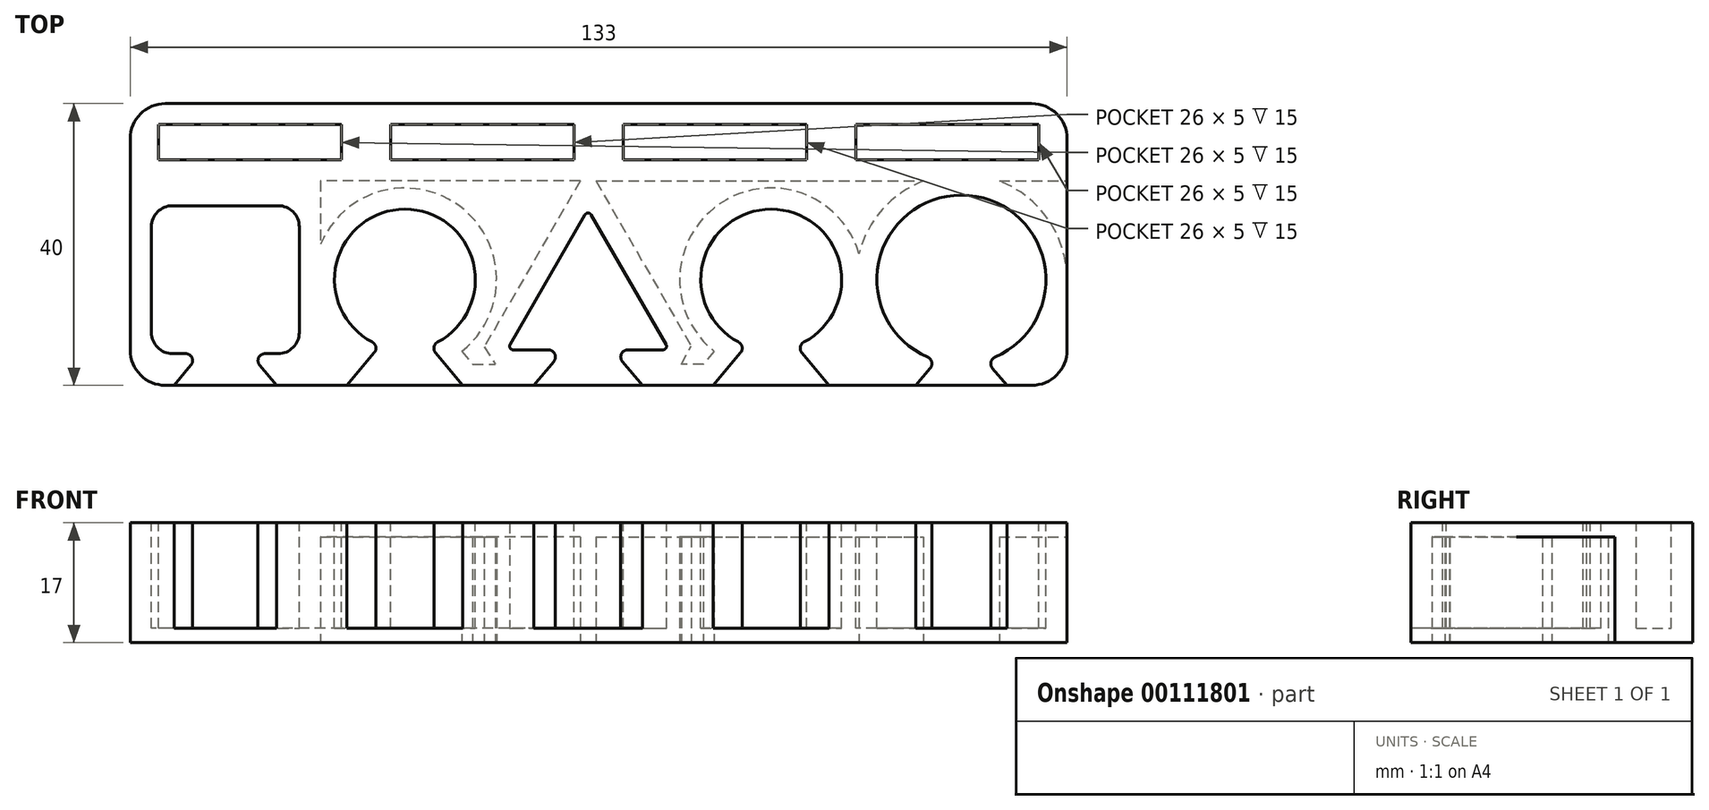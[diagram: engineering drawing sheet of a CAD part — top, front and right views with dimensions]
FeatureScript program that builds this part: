
annotation { "Feature Type Name" : "Feature", "Feature Type Description" : "" }
export const myFeature = defineFeature(function(context is Context, id is Id, definition is map)
    precondition{}
    {
        {
            var Q0;
            Q0=qCreatedBy(makeId("Top.planeOp"),FACE);
            var sketch = newSketch(context, id + "F0", { "sketchPlane" : qUnion([Q0])});
            skLineSegment(sketch, "E0.bottom", {"start": v(66.5, 20) * mm, "end": v(-66.5, 20) * mm});
            skLineSegment(sketch, "E0.top", {"start": v(66.5, -20) * mm, "end": v(-66.5, -20) * mm});
            skLineSegment(sketch, "E0.left", {"start": v(66.5, 20) * mm, "end": v(66.5, -20) * mm});
            skLineSegment(sketch, "E0.right", {"start": v(-66.5, 20) * mm, "end": v(-66.5, -20) * mm});
            skPoint(sketch, "E0.middle", {"position": v(0, 0) * mm});
            skSolve(sketch);
        }
        {
            var Q0;
            Q0=makeQuery(id+"F0.imprint","IMPRINT",FACE,{"disambiguationData":[TD([[makeQuery(id+"F0.imprint","IMPRINT",EDGE,{"derivedFrom":sQuery(id+"F0.wireOp",EDGE,"E0.bottom")}),1.0]])]});
            extrude(context, id + "F1", {"entities" : qUnion([Q0]), "depth" : 17 * mm});
        }
        {
            var Q0;
            Q0=makeQuery(id+"F1.opExtrude","CAP_FACE",FACE,{"disambiguationData":[OSD([sQuery(id+"F0.wireOp",EDGE,"E0.bottom"),sQuery(id+"F0.wireOp",EDGE,"E0.top"),sQuery(id+"F0.wireOp",EDGE,"E0.left"),sQuery(id+"F0.wireOp",EDGE,"E0.right")])],"isStart":false});
            var sketch = newSketch(context, id + "F2", { "sketchPlane" : qUnion([Q0])});
            skLineSegment(sketch, "E1.bottom", {"start": v(-36.5, 12) * mm, "end": v(-62.5, 12) * mm});
            skLineSegment(sketch, "E1.top", {"start": v(-36.5, 17) * mm, "end": v(-62.5, 17) * mm});
            skLineSegment(sketch, "E1.left", {"start": v(-36.5, 12) * mm, "end": v(-36.5, 17) * mm});
            skLineSegment(sketch, "E1.right", {"start": v(-62.5, 12) * mm, "end": v(-62.5, 17) * mm});
            skPoint(sketch, "E1.middle", {"position": v(-49.5, 14.5) * mm});
            skLineSegment(sketch, "E2.bottom", {"start": v(-3.5, 12) * mm, "end": v(-29.5, 12) * mm});
            skLineSegment(sketch, "E2.top", {"start": v(-3.5, 17) * mm, "end": v(-29.5, 17) * mm});
            skLineSegment(sketch, "E2.left", {"start": v(-3.5, 12) * mm, "end": v(-3.5, 17) * mm});
            skLineSegment(sketch, "E2.right", {"start": v(-29.5, 12) * mm, "end": v(-29.5, 17) * mm});
            skPoint(sketch, "E2.middle", {"position": v(-16.5, 14.5) * mm});
            skLineSegment(sketch, "E3.bottom", {"start": v(29.5, 12) * mm, "end": v(3.5, 12) * mm});
            skLineSegment(sketch, "E3.top", {"start": v(29.5, 17) * mm, "end": v(3.5, 17) * mm});
            skLineSegment(sketch, "E3.left", {"start": v(29.5, 12) * mm, "end": v(29.5, 17) * mm});
            skLineSegment(sketch, "E3.right", {"start": v(3.5, 12) * mm, "end": v(3.5, 17) * mm});
            skPoint(sketch, "E3.middle", {"position": v(16.5, 14.5) * mm});
            skLineSegment(sketch, "E4.bottom", {"start": v(62.5, 12) * mm, "end": v(36.5, 12) * mm});
            skLineSegment(sketch, "E4.top", {"start": v(62.5, 17) * mm, "end": v(36.5, 17) * mm});
            skLineSegment(sketch, "E4.left", {"start": v(62.5, 12) * mm, "end": v(62.5, 17) * mm});
            skLineSegment(sketch, "E4.right", {"start": v(36.5, 12) * mm, "end": v(36.5, 17) * mm});
            skPoint(sketch, "E4.middle", {"position": v(49.5, 14.5) * mm});
            skLineSegment(sketch, "E5.bottom", {"start": v(-42.5, -15.5) * mm, "end": v(-63.5, -15.5) * mm});
            skLineSegment(sketch, "E5.top", {"start": v(-42.5, 5.5) * mm, "end": v(-63.5, 5.5) * mm});
            skLineSegment(sketch, "E5.left", {"start": v(-42.5, -15.5) * mm, "end": v(-42.5, 5.5) * mm});
            skLineSegment(sketch, "E5.right", {"start": v(-63.5, -15.5) * mm, "end": v(-63.5, 5.5) * mm});
            skPoint(sketch, "E5.middle", {"position": v(-53, -5) * mm});
            skCircle(sketch, "E6", {"center": v(-27.5, -5) * mm, "radius": 10 * mm});
            skCircle(sketch, "E7", {"center": v(24.5, -5) * mm, "radius": 10 * mm});
            skCircle(sketch, "E8", {"center": v(51.5, -5) * mm, "radius": 12 * mm});
            skLineSegment(sketch, "E9", {"start": v(-13, -14.96) * mm, "end": v(10, -14.96) * mm});
            skLineSegment(sketch, "E10", {"start": v(-1.5, -14.96) * mm, "end": v(-1.5, 4.96) * mm});
            skLineSegment(sketch, "E11", {"start": v(-1.5, 4.96) * mm, "end": v(10, -14.96) * mm});
            skLineSegment(sketch, "E12", {"start": v(-1.5, 4.96) * mm, "end": v(-13, -14.96) * mm});
            skLineSegment(sketch, "E13", {"start": v(-49.5, -15.5) * mm, "end": v(-45.72, -20) * mm});
            skLineSegment(sketch, "E14", {"start": v(-56.5, -15.5) * mm, "end": v(-60.28, -20) * mm});
            skLineSegment(sketch, "E15", {"start": v(-31, -14.37) * mm, "end": v(-35.73, -20) * mm});
            skLineSegment(sketch, "E16", {"start": v(-24, -14.37) * mm, "end": v(-19.27, -20) * mm});
            skLineSegment(sketch, "E17", {"start": v(-5, -14.96) * mm, "end": v(-9.23, -20) * mm});
            skLineSegment(sketch, "E18", {"start": v(2, -14.96) * mm, "end": v(6.23, -20) * mm});
            skLineSegment(sketch, "E19", {"start": v(21, -14.37) * mm, "end": v(16.27, -20) * mm});
            skLineSegment(sketch, "E20", {"start": v(28, -14.37) * mm, "end": v(32.73, -20) * mm});
            skLineSegment(sketch, "E21", {"start": v(48, -16.48) * mm, "end": v(45.04, -20) * mm});
            skLineSegment(sketch, "E22", {"start": v(55, -16.48) * mm, "end": v(57.96, -20) * mm});
            skSolve(sketch);
        }
        {
            var Q0;
            Q0=makeQuery(id+"F2.imprint","IMPRINT",FACE,{"disambiguationData":[TD([[makeQuery(id+"F2.imprint","IMPRINT",EDGE,{"derivedFrom":sQuery(id+"F2.wireOp",EDGE,"E2.bottom")}),-1.0]])]});
            var Q1;
            Q1=makeQuery(id+"F2.imprint","IMPRINT",FACE,{"disambiguationData":[TD([[makeQuery(id+"F2.imprint","IMPRINT",EDGE,{"derivedFrom":sQuery(id+"F2.wireOp",EDGE,"E3.bottom")}),-1.0]])]});
            var Q2;
            Q2=makeQuery(id+"F2.imprint","IMPRINT",FACE,{"disambiguationData":[TD([[makeQuery(id+"F2.imprint","IMPRINT",EDGE,{"derivedFrom":sQuery(id+"F2.wireOp",EDGE,"E4.bottom")}),-1.0]])]});
            var Q3;
            Q3=makeQuery(id+"F2.imprint","IMPRINT",FACE,{"disambiguationData":[TD([[makeQuery(id+"F2.imprint","IMPRINT",EDGE,{"derivedFrom":sQuery(id+"F2.wireOp",EDGE,"E5.top")}),1.0]])]});
            var Q4;
            {var subQ0=sQuery(id+"F2.wireOp",EDGE,"E6");var subQ1=makeQuery(id+"F2.imprint","INTERSECT",VERTEX,{"derivedFrom":[subQ0,sQuery(id+"F2.wireOp",EDGE,"E15")]});Q4=makeQuery(id+"F2.imprint","IMPRINT",FACE,{"disambiguationData":[TD([[makeQuery(id+"F2.imprint","IMPRINT",EDGE,{"disambiguationData":[TD([[subQ1,-1.0]])],"derivedFrom":subQ0}),1.0]])]});}
            var Q5;
            {var subQ0=sQuery(id+"F2.wireOp",EDGE,"E7");var subQ1=makeQuery(id+"F2.imprint","INTERSECT",VERTEX,{"derivedFrom":[subQ0,sQuery(id+"F2.wireOp",EDGE,"E19")]});Q5=makeQuery(id+"F2.imprint","IMPRINT",FACE,{"disambiguationData":[TD([[makeQuery(id+"F2.imprint","IMPRINT",EDGE,{"disambiguationData":[TD([[subQ1,-1.0]])],"derivedFrom":subQ0}),1.0]])]});}
            var Q6;
            {var subQ0=sQuery(id+"F2.wireOp",EDGE,"E8");var subQ1=makeQuery(id+"F2.imprint","INTERSECT",VERTEX,{"derivedFrom":[subQ0,sQuery(id+"F2.wireOp",EDGE,"E21")]});Q6=makeQuery(id+"F2.imprint","IMPRINT",FACE,{"disambiguationData":[TD([[makeQuery(id+"F2.imprint","IMPRINT",EDGE,{"disambiguationData":[TD([[subQ1,-1.0]])],"derivedFrom":subQ0}),1.0]])]});}
            var Q7;
            {var subQ3=sQuery(id+"F2.wireOp",EDGE,"E10");Q7=makeQuery(id+"F2.imprint","IMPRINT",FACE,{"disambiguationData":[TD([[makeQuery(id+"F2.imprint","IMPRINT",EDGE,{"derivedFrom":subQ3}),1.0]])]});}
            var Q8;
            {var subQ0=sQuery(id+"F2.wireOp",EDGE,"E10");Q8=makeQuery(id+"F2.imprint","IMPRINT",FACE,{"disambiguationData":[TD([[makeQuery(id+"F2.imprint","IMPRINT",EDGE,{"derivedFrom":subQ0}),-1.0]])]});}
            var Q9;
            Q9=makeQuery(id+"F2.imprint","IMPRINT",FACE,{"disambiguationData":[TD([[makeQuery(id+"F2.imprint","IMPRINT",EDGE,{"derivedFrom":sQuery(id+"F2.wireOp",EDGE,"E1.bottom")}),-1.0]])]});
            var Q10;
            {var subQ0=sQuery(id+"F2.wireOp",EDGE,"E13");Q10=makeQuery(id+"F2.imprint","IMPRINT",FACE,{"disambiguationData":[TD([[makeQuery(id+"F2.imprint","IMPRINT",EDGE,{"derivedFrom":subQ0}),-1.0]])]});}
            var Q11;
            {var subQ0=sQuery(id+"F2.wireOp",EDGE,"E15");Q11=makeQuery(id+"F2.imprint","IMPRINT",FACE,{"disambiguationData":[TD([[makeQuery(id+"F2.imprint","IMPRINT",EDGE,{"derivedFrom":subQ0}),1.0]])]});}
            var Q12;
            {var subQ3=sQuery(id+"F2.wireOp",EDGE,"E17");Q12=makeQuery(id+"F2.imprint","IMPRINT",FACE,{"disambiguationData":[TD([[makeQuery(id+"F2.imprint","IMPRINT",EDGE,{"derivedFrom":subQ3}),1.0]])]});}
            var Q13;
            {var subQ0=sQuery(id+"F2.wireOp",EDGE,"E19");Q13=makeQuery(id+"F2.imprint","IMPRINT",FACE,{"disambiguationData":[TD([[makeQuery(id+"F2.imprint","IMPRINT",EDGE,{"derivedFrom":subQ0}),1.0]])]});}
            var Q14;
            {var subQ0=sQuery(id+"F2.wireOp",EDGE,"E21");Q14=makeQuery(id+"F2.imprint","IMPRINT",FACE,{"disambiguationData":[TD([[makeQuery(id+"F2.imprint","IMPRINT",EDGE,{"derivedFrom":subQ0}),1.0]])]});}
            extrude(context, id + "F3", {"entities" : qUnion([Q0, Q1, Q2, Q3, Q4, Q5, Q6, Q7, Q8, Q9, Q10, Q11, Q12, Q13, Q14]), "operationType" : NewBodyOperationType.REMOVE, "oppositeDirection" : true, "depth" : 15 * mm});
        }
        {
            var Q0;
            Q0=makeQuery(id+"F3.boolean.opBoolean","COPY",EDGE,{"derivedFrom":makeQuery(id+"F3.opExtrude","SWEPT_EDGE",EDGE,{"disambiguationData":[OSD([sQuery(id+"F2.wireOp",EDGE,"E7"),sQuery(id+"F2.wireOp",EDGE,"E19")])]})});
            var Q1;
            Q1=makeQuery(id+"F3.boolean.opBoolean","COPY",EDGE,{"derivedFrom":makeQuery(id+"F3.opExtrude","SWEPT_EDGE",EDGE,{"disambiguationData":[OSD([sQuery(id+"F2.wireOp",EDGE,"E7"),sQuery(id+"F2.wireOp",EDGE,"E20")])]})});
            var Q2;
            Q2=makeQuery(id+"F3.boolean.opBoolean","COPY",EDGE,{"derivedFrom":makeQuery(id+"F3.opExtrude","SWEPT_EDGE",EDGE,{"disambiguationData":[OSD([sQuery(id+"F2.wireOp",EDGE,"E8"),sQuery(id+"F2.wireOp",EDGE,"E22")])]})});
            var Q3;
            Q3=makeQuery(id+"F3.boolean.opBoolean","COPY",EDGE,{"derivedFrom":makeQuery(id+"F3.opExtrude","SWEPT_EDGE",EDGE,{"disambiguationData":[OSD([sQuery(id+"F0.wireOp",EDGE,"E0.top"),sQuery(id+"F2.wireOp",EDGE,"E22")])]})});
            var Q4;
            Q4=makeQuery(id+"F3.boolean.opBoolean","COPY",EDGE,{"derivedFrom":makeQuery(id+"F3.opExtrude","SWEPT_EDGE",EDGE,{"disambiguationData":[OSD([sQuery(id+"F0.wireOp",EDGE,"E0.top"),sQuery(id+"F2.wireOp",EDGE,"E21")])]})});
            var Q5;
            Q5=makeQuery(id+"F3.boolean.opBoolean","COPY",EDGE,{"derivedFrom":makeQuery(id+"F3.opExtrude","SWEPT_EDGE",EDGE,{"disambiguationData":[OSD([sQuery(id+"F2.wireOp",EDGE,"E8"),sQuery(id+"F2.wireOp",EDGE,"E21")])]})});
            var Q6;
            Q6=makeQuery(id+"F3.boolean.opBoolean","COPY",EDGE,{"derivedFrom":makeQuery(id+"F3.opExtrude","SWEPT_EDGE",EDGE,{"disambiguationData":[OSD([sQuery(id+"F0.wireOp",EDGE,"E0.top"),sQuery(id+"F2.wireOp",EDGE,"E20")])]})});
            var Q7;
            Q7=makeQuery(id+"F3.boolean.opBoolean","COPY",EDGE,{"derivedFrom":makeQuery(id+"F3.opExtrude","SWEPT_EDGE",EDGE,{"disambiguationData":[OSD([sQuery(id+"F0.wireOp",EDGE,"E0.top"),sQuery(id+"F2.wireOp",EDGE,"E19")])]})});
            var Q8;
            Q8=makeQuery(id+"F3.boolean.opBoolean","COPY",EDGE,{"derivedFrom":makeQuery(id+"F3.opExtrude","SWEPT_EDGE",EDGE,{"disambiguationData":[OSD([sQuery(id+"F0.wireOp",EDGE,"E0.top"),sQuery(id+"F2.wireOp",EDGE,"E18")])]})});
            var Q9;
            Q9=makeQuery(id+"F3.boolean.opBoolean","COPY",EDGE,{"derivedFrom":makeQuery(id+"F3.opExtrude","SWEPT_EDGE",EDGE,{"disambiguationData":[OSD([sQuery(id+"F2.wireOp",EDGE,"E9"),sQuery(id+"F2.wireOp",EDGE,"E18")])]})});
            var Q10;
            Q10=makeQuery(id+"F3.boolean.opBoolean","COPY",EDGE,{"derivedFrom":makeQuery(id+"F3.opExtrude","SWEPT_EDGE",EDGE,{"disambiguationData":[OSD([sQuery(id+"F2.wireOp",EDGE,"E9"),sQuery(id+"F2.wireOp",EDGE,"E17")])]})});
            var Q11;
            Q11=makeQuery(id+"F3.boolean.opBoolean","COPY",EDGE,{"derivedFrom":makeQuery(id+"F3.opExtrude","SWEPT_EDGE",EDGE,{"disambiguationData":[OSD([sQuery(id+"F0.wireOp",EDGE,"E0.top"),sQuery(id+"F2.wireOp",EDGE,"E17")])]})});
            var Q12;
            Q12=makeQuery(id+"F3.boolean.opBoolean","COPY",EDGE,{"derivedFrom":makeQuery(id+"F3.opExtrude","SWEPT_EDGE",EDGE,{"disambiguationData":[OSD([sQuery(id+"F2.wireOp",EDGE,"E6"),sQuery(id+"F2.wireOp",EDGE,"E16")])]})});
            var Q13;
            Q13=makeQuery(id+"F3.boolean.opBoolean","COPY",EDGE,{"derivedFrom":makeQuery(id+"F3.opExtrude","SWEPT_EDGE",EDGE,{"disambiguationData":[OSD([sQuery(id+"F0.wireOp",EDGE,"E0.top"),sQuery(id+"F2.wireOp",EDGE,"E16")])]})});
            var Q14;
            Q14=makeQuery(id+"F3.boolean.opBoolean","COPY",EDGE,{"derivedFrom":makeQuery(id+"F3.opExtrude","SWEPT_EDGE",EDGE,{"disambiguationData":[OSD([sQuery(id+"F2.wireOp",EDGE,"E6"),sQuery(id+"F2.wireOp",EDGE,"E15")])]})});
            var Q15;
            Q15=makeQuery(id+"F3.boolean.opBoolean","COPY",EDGE,{"derivedFrom":makeQuery(id+"F3.opExtrude","SWEPT_EDGE",EDGE,{"disambiguationData":[OSD([sQuery(id+"F0.wireOp",EDGE,"E0.top"),sQuery(id+"F2.wireOp",EDGE,"E15")])]})});
            var Q16;
            Q16=makeQuery(id+"F3.boolean.opBoolean","COPY",EDGE,{"derivedFrom":makeQuery(id+"F3.opExtrude","SWEPT_EDGE",EDGE,{"disambiguationData":[OSD([sQuery(id+"F2.wireOp",EDGE,"E5.bottom"),sQuery(id+"F2.wireOp",EDGE,"E14")])]})});
            var Q17;
            Q17=makeQuery(id+"F3.boolean.opBoolean","COPY",EDGE,{"derivedFrom":makeQuery(id+"F3.opExtrude","SWEPT_EDGE",EDGE,{"disambiguationData":[OSD([sQuery(id+"F0.wireOp",EDGE,"E0.top"),sQuery(id+"F2.wireOp",EDGE,"E14")])]})});
            var Q18;
            Q18=makeQuery(id+"F3.boolean.opBoolean","COPY",EDGE,{"derivedFrom":makeQuery(id+"F3.opExtrude","SWEPT_EDGE",EDGE,{"disambiguationData":[OSD([sQuery(id+"F2.wireOp",EDGE,"E5.bottom"),sQuery(id+"F2.wireOp",EDGE,"E13")])]})});
            var Q19;
            Q19=makeQuery(id+"F3.boolean.opBoolean","COPY",EDGE,{"derivedFrom":makeQuery(id+"F3.opExtrude","SWEPT_EDGE",EDGE,{"disambiguationData":[OSD([sQuery(id+"F0.wireOp",EDGE,"E0.top"),sQuery(id+"F2.wireOp",EDGE,"E13")])]})});
            fillet(context, id + "F4", {"entities" : qUnion([Q0, Q1, Q2, Q3, Q4, Q5, Q6, Q7, Q8, Q9, Q10, Q11, Q12, Q13, Q14, Q15, Q16, Q17, Q18, Q19]), "radius" : 1 * mm, "tangentPropagation" : true, "allowEdgeOverflow" : false});
        }
        {
            var Q0;
            Q0=makeQuery(id+"F3.boolean.opBoolean","COPY",EDGE,{"derivedFrom":makeQuery(id+"F3.opExtrude","SWEPT_EDGE",EDGE,{"disambiguationData":[OSD([sQuery(id+"F2.wireOp",EDGE,"E10"),sQuery(id+"F2.wireOp",EDGE,"E11"),sQuery(id+"F2.wireOp",EDGE,"E12")])]})});
            var Q1;
            Q1=makeQuery(id+"F3.boolean.opBoolean","COPY",EDGE,{"derivedFrom":makeQuery(id+"F3.opExtrude","SWEPT_EDGE",EDGE,{"disambiguationData":[OSD([sQuery(id+"F2.wireOp",EDGE,"E9"),sQuery(id+"F2.wireOp",EDGE,"E12")])]})});
            var Q2;
            Q2=makeQuery(id+"F3.boolean.opBoolean","COPY",EDGE,{"derivedFrom":makeQuery(id+"F3.opExtrude","SWEPT_EDGE",EDGE,{"disambiguationData":[OSD([sQuery(id+"F2.wireOp",EDGE,"E9"),sQuery(id+"F2.wireOp",EDGE,"E11")])]})});
            fillet(context, id + "F5", {"entities" : qUnion([Q0, Q1, Q2]), "radius" : 0.5 * mm, "tangentPropagation" : true, "allowEdgeOverflow" : false});
        }
        {
            var Q0;
            Q0=makeQuery(id+"F1.opExtrude","SWEPT_EDGE",EDGE,{"disambiguationData":[OSD([sQuery(id+"F0.wireOp",EDGE,"E0.top"),sQuery(id+"F0.wireOp",EDGE,"E0.right")])]});
            var Q1;
            Q1=makeQuery(id+"F1.opExtrude","SWEPT_EDGE",EDGE,{"disambiguationData":[OSD([sQuery(id+"F0.wireOp",EDGE,"E0.bottom"),sQuery(id+"F0.wireOp",EDGE,"E0.right")])]});
            var Q2;
            Q2=makeQuery(id+"F1.opExtrude","SWEPT_EDGE",EDGE,{"disambiguationData":[OSD([sQuery(id+"F0.wireOp",EDGE,"E0.top"),sQuery(id+"F0.wireOp",EDGE,"E0.left")])]});
            var Q3;
            Q3=makeQuery(id+"F1.opExtrude","SWEPT_EDGE",EDGE,{"disambiguationData":[OSD([sQuery(id+"F0.wireOp",EDGE,"E0.bottom"),sQuery(id+"F0.wireOp",EDGE,"E0.left")])]});
            fillet(context, id + "F6", {"entities" : qUnion([Q0, Q1, Q2, Q3]), "radius" : 5 * mm, "tangentPropagation" : true, "allowEdgeOverflow" : false});
        }
        {
            var Q0;
            Q0=makeQuery(id+"F3.boolean.opBoolean","COPY",EDGE,{"derivedFrom":makeQuery(id+"F3.opExtrude","SWEPT_EDGE",EDGE,{"disambiguationData":[OSD([sQuery(id+"F2.wireOp",EDGE,"E5.top"),sQuery(id+"F2.wireOp",EDGE,"E5.left")])]})});
            var Q1;
            Q1=makeQuery(id+"F3.boolean.opBoolean","COPY",EDGE,{"derivedFrom":makeQuery(id+"F3.opExtrude","SWEPT_EDGE",EDGE,{"disambiguationData":[OSD([sQuery(id+"F2.wireOp",EDGE,"E5.top"),sQuery(id+"F2.wireOp",EDGE,"E5.right")])]})});
            var Q2;
            Q2=makeQuery(id+"F3.boolean.opBoolean","COPY",EDGE,{"derivedFrom":makeQuery(id+"F3.opExtrude","SWEPT_EDGE",EDGE,{"disambiguationData":[OSD([sQuery(id+"F2.wireOp",EDGE,"E5.bottom"),sQuery(id+"F2.wireOp",EDGE,"E5.right")])]})});
            var Q3;
            Q3=makeQuery(id+"F3.boolean.opBoolean","COPY",EDGE,{"derivedFrom":makeQuery(id+"F3.opExtrude","SWEPT_EDGE",EDGE,{"disambiguationData":[OSD([sQuery(id+"F2.wireOp",EDGE,"E5.bottom"),sQuery(id+"F2.wireOp",EDGE,"E5.left")])]})});
            fillet(context, id + "F7", {"entities" : qUnion([Q0, Q1, Q2, Q3]), "radius" : 3 * mm, "tangentPropagation" : true, "allowEdgeOverflow" : false});
        }
        {
            var Q0;
            Q0=makeQuery(id+"F1.opExtrude","CAP_FACE",FACE,{"disambiguationData":[OSD([sQuery(id+"F0.wireOp",EDGE,"E0.bottom"),sQuery(id+"F0.wireOp",EDGE,"E0.top"),sQuery(id+"F0.wireOp",EDGE,"E0.left"),sQuery(id+"F0.wireOp",EDGE,"E0.right")])],"isStart":false});
            var sketch = newSketch(context, id + "F8", { "sketchPlane" : qUnion([Q0])});
            skCircle(sketch, "E23", {"center": v(-27.5, -5) * mm, "radius": 13 * mm});
            skLineSegment(sketch, "E24", {"start": v(-2.63, 9) * mm, "end": v(-16.23, -14.55) * mm});
            skLineSegment(sketch, "E25", {"start": v(-19.42, -15.16) * mm, "end": v(-17.87, -17) * mm});
            skLineSegment(sketch, "E26", {"start": v(-17.87, -17) * mm, "end": v(-14.66, -17) * mm});
            skLineSegment(sketch, "E27", {"start": v(-16.23, -14.55) * mm, "end": v(-14.66, -17) * mm});
            skLineSegment(sketch, "E28", {"start": v(-2.63, 9) * mm, "end": v(-39.5, 9) * mm});
            skLineSegment(sketch, "E29", {"start": v(-2.63, 9) * mm, "end": v(66.5, 9) * mm});
            skLineSegment(sketch, "E30", {"start": v(-0.37, 9) * mm, "end": v(13.16, -14.43) * mm});
            skCircle(sketch, "E31", {"center": v(24.5, -5) * mm, "radius": 13 * mm});
            skLineSegment(sketch, "E32", {"start": v(16.4, -15.17) * mm, "end": v(14.87, -17) * mm});
            skLineSegment(sketch, "E33", {"start": v(14.87, -17) * mm, "end": v(11.72, -17) * mm});
            skLineSegment(sketch, "E34", {"start": v(11.72, -17) * mm, "end": v(13.16, -14.43) * mm});
            skLineSegment(sketch, "E35", {"start": v(-39.5, 9) * mm, "end": v(-39.5, 0) * mm});
            skCircle(sketch, "E36", {"center": v(51.5, -5) * mm, "radius": 15 * mm});
            skPoint(sketch, "E37", {"position": v(13.5, 9) * mm});
            skSolve(sketch);
        }
        {
            var Q0;
            Q0=makeQuery(id+"F1.opExtrude","CAP_FACE",FACE,{"disambiguationData":[OSD([sQuery(id+"F0.wireOp",EDGE,"E0.bottom"),sQuery(id+"F0.wireOp",EDGE,"E0.top"),sQuery(id+"F0.wireOp",EDGE,"E0.left"),sQuery(id+"F0.wireOp",EDGE,"E0.right")])],"isStart":true});
            var sketch = newSketch(context, id + "F9", { "sketchPlane" : qUnion([Q0])});
            skLineSegment(sketch, "E38.0", {"start": v(-2.63, -9) * mm, "end": v(-16.23, 14.55) * mm});
            skLineSegment(sketch, "E39.0", {"start": v(-16.23, 14.55) * mm, "end": v(-14.66, 17) * mm});
            skLineSegment(sketch, "E40.0", {"start": v(-17.87, 17) * mm, "end": v(-14.66, 17) * mm});
            skLineSegment(sketch, "E41.0", {"start": v(-19.42, 15.16) * mm, "end": v(-17.87, 17) * mm});
            skCircle(sketch, "E42.0", {"center": v(-27.5, 5) * mm, "radius": 13 * mm});
            skLineSegment(sketch, "E43.0", {"start": v(-39.5, -9) * mm, "end": v(-39.5, 0) * mm});
            skLineSegment(sketch, "E44.0", {"start": v(-2.63, -9) * mm, "end": v(-39.5, -9) * mm});
            skLineSegment(sketch, "E45.0", {"start": v(-2.63, -9) * mm, "end": v(66.5, -9) * mm});
            skLineSegment(sketch, "E46.0", {"start": v(-0.37, -9) * mm, "end": v(13.16, 14.43) * mm});
            skLineSegment(sketch, "E47.0", {"start": v(11.72, 17) * mm, "end": v(13.16, 14.43) * mm});
            skLineSegment(sketch, "E48.0", {"start": v(14.87, 17) * mm, "end": v(11.72, 17) * mm});
            skLineSegment(sketch, "E49.0", {"start": v(16.4, 15.17) * mm, "end": v(14.87, 17) * mm});
            skCircle(sketch, "E50.0", {"center": v(24.5, 5) * mm, "radius": 13 * mm});
            skCircle(sketch, "E51.0", {"center": v(51.5, 5) * mm, "radius": 15 * mm});
            skSolve(sketch);
        }
        {
            var Q0;
            Q0=makeQuery(id+"F9.imprint","IMPRINT",FACE,{"disambiguationData":[TD([[makeQuery(id+"F9.imprint","IMPRINT",EDGE,{"derivedFrom":sQuery(id+"F9.wireOp",EDGE,"E38.0")}),1.0]])]});
            var Q1;
            {var subQ0=sQuery(id+"F9.wireOp",EDGE,"E46.0");Q1=makeQuery(id+"F9.imprint","IMPRINT",FACE,{"disambiguationData":[TD([[makeQuery(id+"F9.imprint","IMPRINT",EDGE,{"derivedFrom":subQ0}),-1.0]])]});}
            var Q2;
            {var subQ0=sQuery(id+"F9.wireOp",EDGE,"E45.0");var subQ1=makeQuery(id+"F1.opExtrude","CAP_EDGE",EDGE,{"disambiguationData":[OSD([sQuery(id+"F0.wireOp",EDGE,"E0.left")])],"isStart":true});var subQ2=makeQuery(id+"F9.imprint","INTERSECT",VERTEX,{"derivedFrom":[subQ1,subQ0]});Q2=makeQuery(id+"F9.imprint","IMPRINT",FACE,{"disambiguationData":[TD([[makeQuery(id+"F9.imprint","IMPRINT",EDGE,{"disambiguationData":[TD([[subQ2,1.0]])],"derivedFrom":subQ0}),1.0]])]});}
            extrude(context, id + "F10", {"entities" : qUnion([Q0, Q1, Q2]), "operationType" : NewBodyOperationType.REMOVE, "oppositeDirection" : true, "depth" : 15 * mm});
        }
    });
